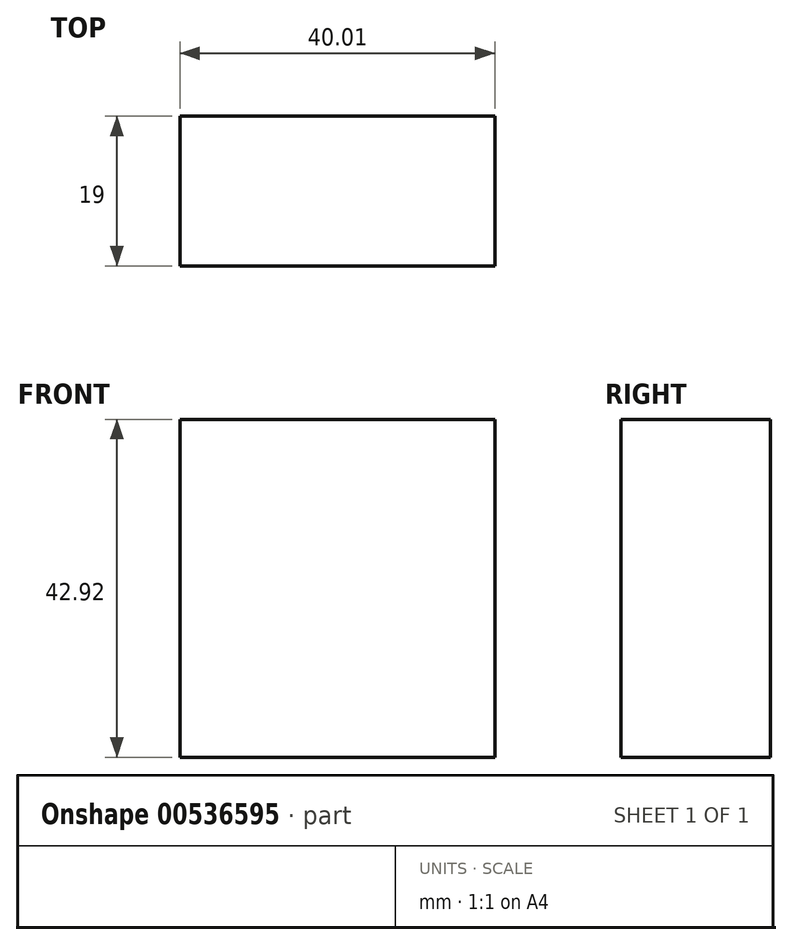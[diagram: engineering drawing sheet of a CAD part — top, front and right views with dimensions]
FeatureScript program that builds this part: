
annotation { "Feature Type Name" : "Feature", "Feature Type Description" : "" }
export const myFeature = defineFeature(function(context is Context, id is Id, definition is map)
    precondition{}
    {
        {
            var Q0;
            Q0=qCreatedBy(makeId("Front.planeOp"),FACE);
            var sketch = newSketch(context, id + "F0", { "sketchPlane" : qUnion([Q0])});
            skLineSegment(sketch, "E0.bottom", {"start": v(-52.36, 32.13) * mm, "end": v(-12.35, 32.13) * mm});
            skLineSegment(sketch, "E0.top", {"start": v(-52.36, -10.8) * mm, "end": v(-12.35, -10.8) * mm});
            skLineSegment(sketch, "E0.left", {"start": v(-52.36, 32.13) * mm, "end": v(-52.36, -10.8) * mm});
            skLineSegment(sketch, "E0.right", {"start": v(-12.35, 32.13) * mm, "end": v(-12.35, -10.8) * mm});
            skSolve(sketch);
        }
        {
            var Q0;
            Q0 = qSketchRegion(id + "F0", true);
            extrude(context, id + "F1", {"entities" : qUnion([Q0]), "depth" : 19 * mm, "offsetDistance" : 25.4 * mm});
        }
    });
